# Revit family: Shower-Valve_Trim-KOHLER-Artifacts-C72770_1
name_source: partatom
category: Specialty Equipment
revit_build: Autodesk Revit 2017 (Build: 20160225_1515(x64)
units: mm (PartAtom-declared; Revit-internal decimal feet)

## family parameters
Cut with Voids When Loaded = No
Host = Face
OmniClass Number = 23.31.25.00
OmniClass Title = Toilet and Bath Specialties
Part Type = Normal
Room Calculation Point = No
Round Connector Dimension = Use Diameter
Shared = No

## types (2) — shared parameters
ADA Compliant = No
Assembly Code = C1030200
Date Modified = 05/27/2021
Default Elevation = 42"
Finish = Kohler-Metal-CP-Polished_Chrome
Height = 4 1/2"
Manufacturer = KOHLER Co.
Master Format 2014 = 10 28 00
Master Format 2014 Name = Toilet, Bath, and Laundry Accessories
Material = Premium Metal Construction
Product Documentation Link = https://resources.kohler.com
Product Name = Artifacts
Product Page URL = https://www.kohler.co.uk
URL = https://www.kohler.co.uk
WaterSense Certified = No
Width = 4 1/2"

## per-type parameters (varying)
| type | Description | Handle Clearance | Length | Lever Handle | Model | Prong Handle | Type |
| Lever Handle, CP-Polished Chrome | Built-in 3-way Diverter Valve, Lever Handle | 3 5/16" | 4 1/2" | Yes | C72770-4-CP | No | 1 |
| Prong Handle, CP- Polished Chrome | Built-in 3-way Diverter Valve, Prong Handle | 1 1/2" | 4 3/4" | No | C72770-3M-CP | Yes | 2 |

## geometry (parser evidence)
native form markers: Sweep x5
no freeform markers — native parametric forms only
